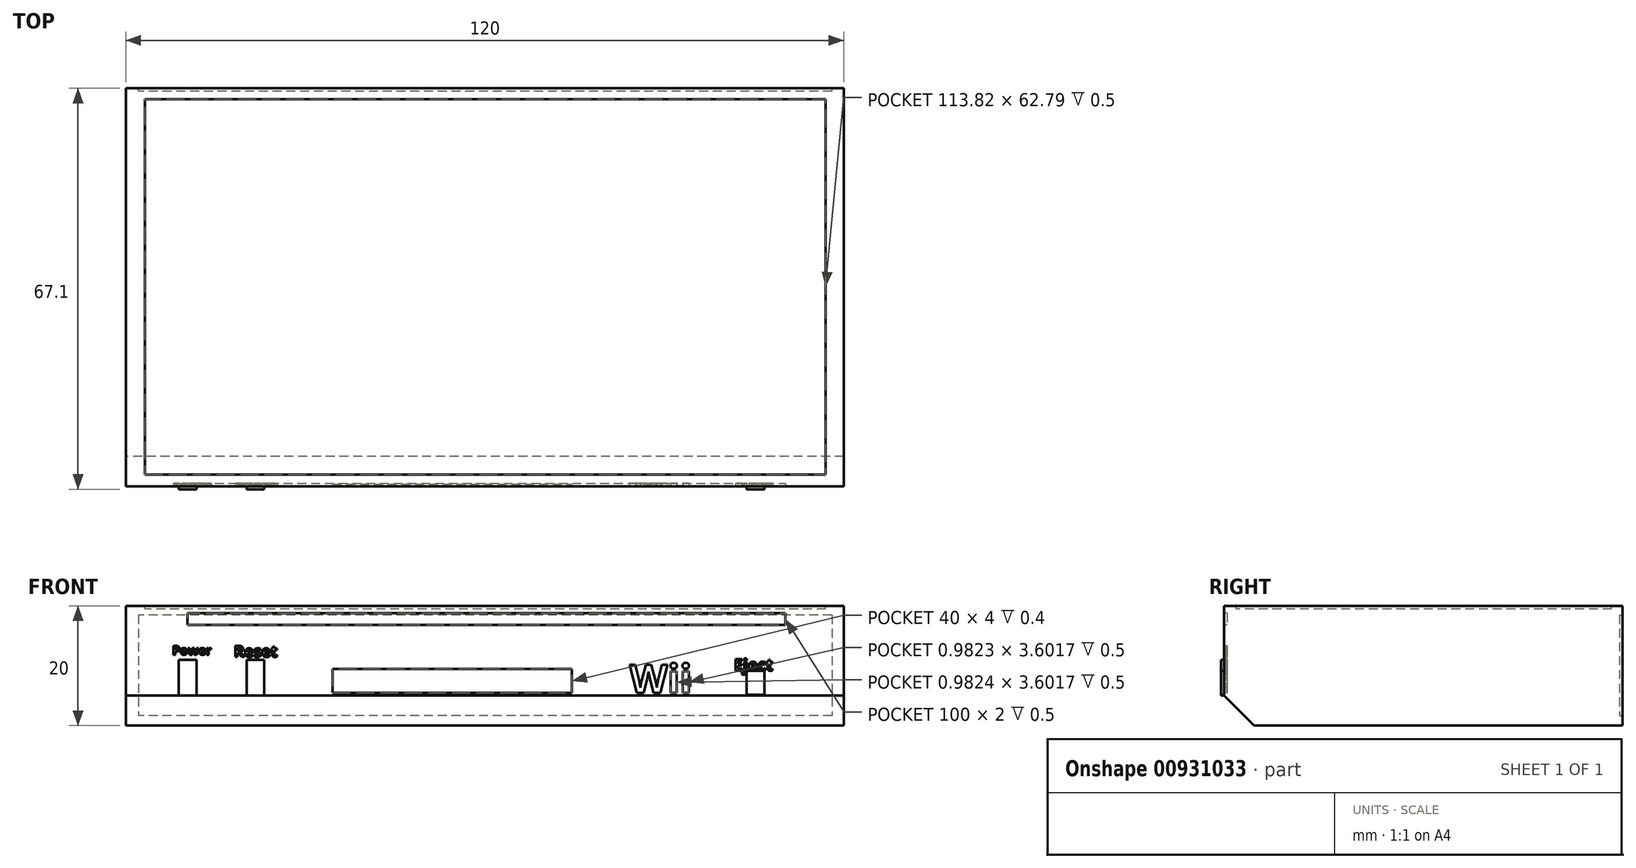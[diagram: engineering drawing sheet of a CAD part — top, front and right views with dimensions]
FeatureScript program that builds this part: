
annotation { "Feature Type Name" : "Feature", "Feature Type Description" : "" }
export const myFeature = defineFeature(function(context is Context, id is Id, definition is map)
    precondition{}
    {
        {
            var Q0;
            Q0=qCreatedBy(makeId("Front.planeOp"),FACE);
            var sketch = newSketch(context, id + "F0", { "sketchPlane" : qUnion([Q0])});
            skLineSegment(sketch, "E0.bottom", {"start": v(-56.39, 34.6) * mm, "end": v(63.61, 34.6) * mm});
            skLineSegment(sketch, "E0.top", {"start": v(-56.39, 14.6) * mm, "end": v(63.61, 14.6) * mm});
            skLineSegment(sketch, "E0.left", {"start": v(-56.39, 34.6) * mm, "end": v(-56.39, 14.6) * mm});
            skLineSegment(sketch, "E0.right", {"start": v(63.61, 34.6) * mm, "end": v(63.61, 14.6) * mm});
            skSolve(sketch);
        }
        {
            var Q0;
            Q0 = qSketchRegion(id + "F0", true);
            extrude(context, id + "F1", {"entities" : qUnion([Q0]), "oppositeDirection" : true, "depth" : 66.6 * mm, "offsetDistance" : 25 * mm});
        }
        {
            var Q0;
            Q0=makeQuery(id+"F1.opExtrude","CAP_EDGE",EDGE,{"disambiguationData":[OSD([sQuery(id+"F0.wireOp",EDGE,"E0.top")])],"isStart":true});
            chamfer(context, id + "F2", {"entities" : qUnion([Q0]), "width" : 5 * mm, "tangentPropagation" : true});
        }
        {
            var Q0;
            Q0=makeQuery(id+"F1.opExtrude","CAP_FACE",FACE,{"disambiguationData":[OSD([sQuery(id+"F0.wireOp",EDGE,"E0.bottom"),sQuery(id+"F0.wireOp",EDGE,"E0.top"),sQuery(id+"F0.wireOp",EDGE,"E0.left"),sQuery(id+"F0.wireOp",EDGE,"E0.right")])],"isStart":true});
            var sketch = newSketch(context, id + "F3", { "sketchPlane" : qUnion([Q0])});
            skLineSegment(sketch, "E1.bottom", {"start": v(-47.57, 25.6) * mm, "end": v(-44.57, 25.6) * mm});
            skLineSegment(sketch, "E1.top", {"start": v(-47.57, 19.6) * mm, "end": v(-44.57, 19.6) * mm});
            skLineSegment(sketch, "E1.left", {"start": v(-47.57, 25.6) * mm, "end": v(-47.57, 19.6) * mm});
            skLineSegment(sketch, "E1.right", {"start": v(-44.57, 25.6) * mm, "end": v(-44.57, 19.6) * mm});
            skLineSegment(sketch, "E2.bottom", {"start": v(-36.23, 25.6) * mm, "end": v(-33.29, 25.6) * mm});
            skLineSegment(sketch, "E2.top", {"start": v(-36.23, 19.6) * mm, "end": v(-33.29, 19.6) * mm});
            skLineSegment(sketch, "E2.left", {"start": v(-36.23, 25.6) * mm, "end": v(-36.23, 19.6) * mm});
            skLineSegment(sketch, "E2.right", {"start": v(-33.29, 25.6) * mm, "end": v(-33.29, 19.6) * mm});
            skSolve(sketch);
        }
        {
            var Q0;
            Q0=makeQuery(id+"F3.imprint","IMPRINT",FACE,{"disambiguationData":[TD([[makeQuery(id+"F3.imprint","IMPRINT",EDGE,{"derivedFrom":sQuery(id+"F3.wireOp",EDGE,"E1.bottom")}),1.0]])]});
            var sketch = newSketch(context, id + "F4", { "sketchPlane" : qUnion([Q0])});
            skLineSegment(sketch, "E3.bottom", {"start": v(-21.83, 24.06) * mm, "end": v(18.17, 24.06) * mm});
            skLineSegment(sketch, "E3.top", {"start": v(-21.83, 20.06) * mm, "end": v(18.17, 20.06) * mm});
            skLineSegment(sketch, "E3.left", {"start": v(-21.83, 24.06) * mm, "end": v(-21.83, 20.06) * mm});
            skLineSegment(sketch, "E3.right", {"start": v(18.17, 24.06) * mm, "end": v(18.17, 20.06) * mm});
            skSolve(sketch);
        }
        {
            var Q0;
            Q0=makeQuery(id+"F4.imprint","IMPRINT",FACE,{"disambiguationData":[TD([[makeQuery(id+"F4.imprint","IMPRINT",EDGE,{"derivedFrom":sQuery(id+"F4.wireOp",EDGE,"E3.bottom")}),1.0]])]});
            var sketch = newSketch(context, id + "F5", { "sketchPlane" : qUnion([Q0])});
            skText(sketch, "E4", { "text": "Wii", "fontName": "OpenSans-Bold.ttf"});
            const initialGuessF5  = {"E4": [0.02779, 0.02006, 1, 0, 0.00475]};
            skSetInitialGuess(sketch, initialGuessF5);
            skSolve(sketch);
        }
        {
            var Q0;
            Q0 = qSketchRegion(id + "F4", true);
            extrude(context, id + "F6", {"entities" : qUnion([Q0]), "operationType" : NewBodyOperationType.REMOVE, "oppositeDirection" : true, "depth" : 0.4 * mm, "offsetDistance" : 25 * mm});
        }
        {
            var Q0;
            Q0 = qSketchRegion(id + "F3", true);
            extrude(context, id + "F7", {"entities" : qUnion([Q0]), "operationType" : NewBodyOperationType.ADD, "depth" : 0.5 * mm, "offsetDistance" : 25 * mm});
        }
        {
            var Q0;
            Q0=makeQuery(id+"F5.imprint","IMPRINT",FACE,{"disambiguationData":[TD([[makeQuery(id+"F5.imprint","IMPRINT",EDGE,{"derivedFrom":sQuery(id+"F5.wireOp",EDGE,"E4.sketch_text.stroke-0")}),1.0]])]});
            var sketch = newSketch(context, id + "F8", { "sketchPlane" : qUnion([Q0])});
            skLineSegment(sketch, "E5.bottom", {"start": v(-46.13, 33.4) * mm, "end": v(53.87, 33.4) * mm});
            skLineSegment(sketch, "E5.top", {"start": v(-46.13, 31.4) * mm, "end": v(53.87, 31.4) * mm});
            skLineSegment(sketch, "E5.left", {"start": v(-46.13, 33.4) * mm, "end": v(-46.13, 31.4) * mm});
            skLineSegment(sketch, "E5.right", {"start": v(53.87, 33.4) * mm, "end": v(53.87, 31.4) * mm});
            skSolve(sketch);
        }
        {
            var Q0;
            Q0=makeQuery(id+"F5.imprint","IMPRINT",FACE,{"disambiguationData":[TD([[makeQuery(id+"F5.imprint","IMPRINT",EDGE,{"derivedFrom":sQuery(id+"F5.wireOp",EDGE,"E4.sketch_text.stroke-0")}),1.0]])]});
            var sketch = newSketch(context, id + "F9", { "sketchPlane" : qUnion([Q0])});
            skText(sketch, "E6", { "text": "Power", "fontName": "OpenSans-Bold.ttf"});
            const initialGuessF9  = {"E6": [-0.04865, 0.02642, 1, 0, 0.0015]};
            skSetInitialGuess(sketch, initialGuessF9);
            skSolve(sketch);
        }
        {
            var Q0;
            Q0 = qSketchRegion(id + "F9", true);
            extrude(context, id + "F10", {"entities" : qUnion([Q0]), "operationType" : NewBodyOperationType.REMOVE, "oppositeDirection" : true, "depth" : 0.5 * mm, "offsetDistance" : 25 * mm});
        }
        {
            var Q0;
            Q0 = qSketchRegion(id + "F5", true);
            extrude(context, id + "F11", {"entities" : qUnion([Q0]), "operationType" : NewBodyOperationType.REMOVE, "oppositeDirection" : true, "depth" : 0.5 * mm, "offsetDistance" : 25 * mm});
        }
        {
            var Q0;
            Q0=makeQuery(id+"F8.imprint","IMPRINT",FACE,{"disambiguationData":[TD([[makeQuery(id+"F8.imprint","IMPRINT",EDGE,{"derivedFrom":sQuery(id+"F8.wireOp",EDGE,"E5.bottom")}),1.0]])]});
            var sketch = newSketch(context, id + "F12", { "sketchPlane" : qUnion([Q0])});
            skText(sketch, "E7", { "text": "Reset", "fontName": "OpenSans-Bold.ttf"});
            const initialGuessF12  = {"E7": [-0.03833, 0.02606, 1, 0, 0.00189]};
            skSetInitialGuess(sketch, initialGuessF12);
            skSolve(sketch);
        }
        {
            var Q0;
            Q0 = qSketchRegion(id + "F12", true);
            extrude(context, id + "F13", {"entities" : qUnion([Q0]), "operationType" : NewBodyOperationType.REMOVE, "oppositeDirection" : true, "depth" : 0.5 * mm, "offsetDistance" : 25 * mm});
        }
        {
            var Q0;
            Q0=makeQuery(id+"F8.imprint","IMPRINT",FACE,{"disambiguationData":[TD([[makeQuery(id+"F8.imprint","IMPRINT",EDGE,{"derivedFrom":sQuery(id+"F8.wireOp",EDGE,"E5.bottom")}),1.0]])]});
            var sketch = newSketch(context, id + "F14", { "sketchPlane" : qUnion([Q0])});
            skLineSegment(sketch, "E8.bottom", {"start": v(47.37, 23.76) * mm, "end": v(50.37, 23.76) * mm});
            skLineSegment(sketch, "E8.top", {"start": v(47.37, 19.76) * mm, "end": v(50.37, 19.76) * mm});
            skLineSegment(sketch, "E8.left", {"start": v(47.37, 23.76) * mm, "end": v(47.37, 19.76) * mm});
            skLineSegment(sketch, "E8.right", {"start": v(50.37, 23.76) * mm, "end": v(50.37, 19.76) * mm});
            skSolve(sketch);
        }
        {
            var Q0;
            Q0 = qSketchRegion(id + "F14", true);
            extrude(context, id + "F15", {"entities" : qUnion([Q0]), "operationType" : NewBodyOperationType.ADD, "depth" : 0.5 * mm, "offsetDistance" : 25 * mm});
        }
        {
            var Q0;
            Q0=makeQuery(id+"F1.opExtrude","SWEPT_FACE",FACE,{"disambiguationData":[OSD([sQuery(id+"F0.wireOp",EDGE,"E0.bottom")])]});
            var sketch = newSketch(context, id + "F16", { "sketchPlane" : qUnion([Q0])});
            skLineSegment(sketch, "E9.bottom", {"start": v(60.59, 64.79) * mm, "end": v(-53.24, 64.79) * mm});
            skLineSegment(sketch, "E9.top", {"start": v(60.59, 2) * mm, "end": v(-53.24, 2) * mm});
            skLineSegment(sketch, "E9.left", {"start": v(60.59, 64.79) * mm, "end": v(60.59, 2) * mm});
            skLineSegment(sketch, "E9.right", {"start": v(-53.24, 64.79) * mm, "end": v(-53.24, 2) * mm});
            skSolve(sketch);
        }
        {
            var Q0;
            Q0 = qSketchRegion(id + "F16", true);
            extrude(context, id + "F17", {"entities" : qUnion([Q0]), "operationType" : NewBodyOperationType.REMOVE, "oppositeDirection" : true, "depth" : 0.5 * mm, "offsetDistance" : 25 * mm});
        }
        {
            var Q0;
            Q0 = qSketchRegion(id + "F8", true);
            extrude(context, id + "F18", {"entities" : qUnion([Q0]), "operationType" : NewBodyOperationType.REMOVE, "oppositeDirection" : true, "depth" : 0.5 * mm, "offsetDistance" : 25 * mm});
        }
        {
            var Q0;
            {var subQ0=sQuery(id+"F0.wireOp",EDGE,"E0.top");var subQ41=sQuery(id+"F0.wireOp",EDGE,"E0.bottom");var subQ42=makeQuery(id+"F1.opExtrude","SWEPT_FACE",FACE,{"disambiguationData":[OSD([subQ41])]});var subQ47=sQuery(id+"F0.wireOp",EDGE,"E0.right");var subQ61=sQuery(id+"F0.wireOp",EDGE,"E0.left");Q0=makeQuery(id+"F13.boolean.opBoolean","SPLIT",FACE,{"disambiguationData":[TD([subQ42])],"derivedFrom":makeQuery(id+"F10.boolean.opBoolean","SPLIT",FACE,{"disambiguationData":[TD([subQ42])],"derivedFrom":makeQuery(id+"F1.opExtrude","CAP_FACE",FACE,{"disambiguationData":[OSD([subQ41,subQ0,subQ61,subQ47])],"isStart":true})})});}
            var sketch = newSketch(context, id + "F19", { "sketchPlane" : qUnion([Q0])});
            skText(sketch, "E10", { "text": "Eject", "fontName": "OpenSans-Bold.ttf"});
            const initialGuessF19  = {"E10": [0.04525, 0.02376, 1, 0, 0.00196]};
            skSetInitialGuess(sketch, initialGuessF19);
            skSolve(sketch);
        }
        {
            var Q0;
            Q0 = qSketchRegion(id + "F19", true);
            extrude(context, id + "F20", {"entities" : qUnion([Q0]), "operationType" : NewBodyOperationType.REMOVE, "oppositeDirection" : true, "depth" : 0.5 * mm, "offsetDistance" : 25 * mm});
        }
        {
            var Q0;
            Q0=makeQuery(id+"F1.opExtrude","CAP_FACE",FACE,{"disambiguationData":[OSD([sQuery(id+"F0.wireOp",EDGE,"E0.bottom"),sQuery(id+"F0.wireOp",EDGE,"E0.top"),sQuery(id+"F0.wireOp",EDGE,"E0.left"),sQuery(id+"F0.wireOp",EDGE,"E0.right")])],"isStart":false});
            var sketch = newSketch(context, id + "F21", { "sketchPlane" : qUnion([Q0])});
            skLineSegment(sketch, "E11.bottom", {"start": v(-61.64, 33.08) * mm, "end": v(54.29, 33.08) * mm});
            skLineSegment(sketch, "E11.top", {"start": v(-61.64, 16.27) * mm, "end": v(54.29, 16.27) * mm});
            skLineSegment(sketch, "E11.left", {"start": v(-61.64, 33.08) * mm, "end": v(-61.64, 16.27) * mm});
            skLineSegment(sketch, "E11.right", {"start": v(54.29, 33.08) * mm, "end": v(54.29, 16.27) * mm});
            skSolve(sketch);
        }
        {
            var Q0;
            Q0 = qSketchRegion(id + "F21", true);
            extrude(context, id + "F22", {"entities" : qUnion([Q0]), "operationType" : NewBodyOperationType.REMOVE, "oppositeDirection" : true, "depth" : 0.5 * mm, "offsetDistance" : 25 * mm});
        }
    });
